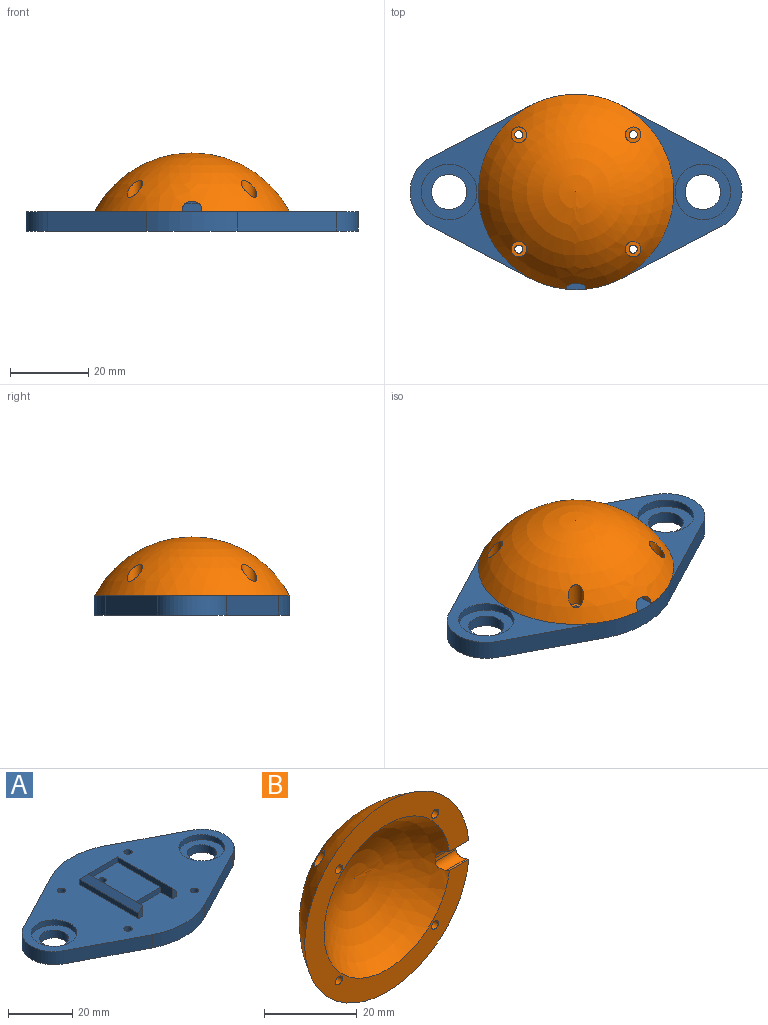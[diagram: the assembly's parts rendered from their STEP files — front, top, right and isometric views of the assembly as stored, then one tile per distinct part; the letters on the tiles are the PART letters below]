
ASSEMBLY  parts=2 mates=1
PART A: 69 faces, bbox 85x50x9 mm
  f0: cylinder r=1.25mm len=5mm, axis (0,0,1), area 39.3mm2, adj f57,f65
  f1: cylinder r=1.25mm len=3mm, axis (0,0,1), area 23.6mm2, adj f5,f50
  f2: cylinder r=1.25mm len=3mm, axis (0,0,1), area 23.6mm2, adj f5,f43
  f3: cylinder r=1.25mm len=3mm, axis (0,0,1), area 23.6mm2, adj f5,f36
  f4: cylinder r=1.25mm len=3mm, axis (0,0,1), area 23.6mm2, adj f5,f29
  f5: plane 85x50mm, normal (0,0,1), area 2120.5mm2, adj f1,f2,f3,f4,f6,f7,f8,f9
  f6: plane 25.58x13.31mm, normal (-0.46,-0.89,0), area 144.2mm2, adj f5,f7,f13,f14
  f7: cylinder r=25mm len=23.08mm, axis (0,0,-1), area 119.9mm2, adj f5,f6,f8,f14
  f8: plane 25.58x13.31mm, normal (0.46,-0.89,0), area 144.2mm2, adj f5,f7,f9,f14
  f9: cylinder r=10mm len=17.74mm, axis (0,0,-1), area 109.1mm2, adj f5,f8,f10,f14
  f10: plane 25.58x13.31mm, normal (0.46,0.89,0), area 144.2mm2, adj f5,f9,f11,f14
  f11: cylinder r=25mm len=23.08mm, axis (0,0,-1), area 119.9mm2, adj f5,f10,f12,f14
  f12: plane 25.58x13.31mm, normal (-0.46,0.89,0), area 144.2mm2, adj f5,f11,f13,f14
  f13: cylinder r=10mm len=17.74mm, axis (0,0,-1), area 109.1mm2, adj f5,f6,f12,f14
  f14: plane 85x50mm, normal (0,0,-1), area 2621.2mm2, adj f6,f7,f8,f9,f10,f11,f12,f13
  f15: cylinder r=4.5mm len=9mm, axis (0,0,1), area 84.8mm2, adj f14,f16
  f16: plane 14.25x14.25mm, normal (0,0,1), area 95.9mm2, adj f15,f17
  f17: cylinder r=7.12mm len=14.25mm, axis (0,0,1), area 89.5mm2, adj f5,f16
  f18: cylinder r=4.5mm len=9mm, axis (0,0,1), area 84.8mm2, adj f14,f19
  f19: plane 14.25x14.25mm, normal (0,0,1), area 95.9mm2, adj f18,f20
  f20: cylinder r=7.12mm len=14.25mm, axis (0,0,1), area 89.5mm2, adj f5,f19
  f21: plane 24x4mm, normal (1,0,0), area 58mm2, adj f5,f22,f28,f64,f65,f66
  f22: plane 13x2mm, normal (0,-1,0), area 26mm2, adj f21,f23,f65,f68
  f23: plane 24x4mm, normal (-1,0,0), area 58mm2, adj f5,f22,f24,f64,f65,f67
  f24: plane 4x2mm, normal (0,-1,0), area 6mm2, adj f5,f23,f25,f67
  f25: plane 26x2mm, normal (1,0,0), area 52mm2, adj f5,f24,f26,f67
  f26: plane 17x2mm, normal (0,1,0), area 34mm2, adj f5,f25,f27,f68
  f27: plane 26x2mm, normal (-1,0,0), area 52mm2, adj f5,f26,f28,f66
  f28: plane 4x2mm, normal (0,-1,0), area 6mm2, adj f5,f21,f27,f66
  f29: plane 5.2x4.5mm, normal (0,0,-1), area 12.6mm2, adj f4,f30,f31,f32,f33,f34,f35
  f30: plane 2.25x2mm, normal (-0.5,-0.87,0), area 5.2mm2, adj f14,f29,f31,f35
  f31: plane 2.6x2mm, normal (-1,0,0), area 5.2mm2, adj f14,f29,f30,f32
  f32: plane 2.25x2mm, normal (-0.5,0.87,0), area 5.2mm2, adj f14,f29,f31,f33
  f33: plane 2.25x2mm, normal (0.5,0.87,0), area 5.2mm2, adj f14,f29,f32,f34
  f34: plane 2.6x2mm, normal (1,0,0), area 5.2mm2, adj f14,f29,f33,f35
  f35: plane 2.25x2mm, normal (0.5,-0.87,0), area 5.2mm2, adj f14,f29,f30,f34
  f36: plane 5.2x4.5mm, normal (0,0,-1), area 12.6mm2, adj f3,f37,f38,f39,f40,f41,f42
  f37: plane 2.25x2mm, normal (-0.5,-0.87,0), area 5.2mm2, adj f14,f36,f38,f42
  f38: plane 2.6x2mm, normal (-1,0,0), area 5.2mm2, adj f14,f36,f37,f39
  f39: plane 2.25x2mm, normal (-0.5,0.87,0), area 5.2mm2, adj f14,f36,f38,f40
  f40: plane 2.25x2mm, normal (0.5,0.87,0), area 5.2mm2, adj f14,f36,f39,f41
  f41: plane 2.6x2mm, normal (1,0,0), area 5.2mm2, adj f14,f36,f40,f42
  f42: plane 2.25x2mm, normal (0.5,-0.87,0), area 5.2mm2, adj f14,f36,f37,f41
  f43: plane 5.2x4.5mm, normal (0,0,-1), area 12.6mm2, adj f2,f44,f45,f46,f47,f48,f49
  f44: plane 2.25x2mm, normal (-0.5,-0.87,0), area 5.2mm2, adj f14,f43,f45,f49
  f45: plane 2.6x2mm, normal (-1,0,0), area 5.2mm2, adj f14,f43,f44,f46
  f46: plane 2.25x2mm, normal (-0.5,0.87,0), area 5.2mm2, adj f14,f43,f45,f47
  f47: plane 2.25x2mm, normal (0.5,0.87,0), area 5.2mm2, adj f14,f43,f46,f48
  f48: plane 2.6x2mm, normal (1,0,0), area 5.2mm2, adj f14,f43,f47,f49
  f49: plane 2.25x2mm, normal (0.5,-0.87,0), area 5.2mm2, adj f14,f43,f44,f48
  f50: plane 5.2x4.5mm, normal (0,0,-1), area 12.6mm2, adj f1,f51,f52,f53,f54,f55,f56
  f51: plane 2.25x2mm, normal (-0.5,-0.87,0), area 5.2mm2, adj f14,f50,f52,f56
  f52: plane 2.6x2mm, normal (-1,0,0), area 5.2mm2, adj f14,f50,f51,f53
  f53: plane 2.25x2mm, normal (-0.5,0.87,0), area 5.2mm2, adj f14,f50,f52,f54
  f54: plane 2.25x2mm, normal (0.5,0.87,0), area 5.2mm2, adj f14,f50,f53,f55
  f55: plane 2.6x2mm, normal (1,0,0), area 5.2mm2, adj f14,f50,f54,f56
  f56: plane 2.25x2mm, normal (0.5,-0.87,0), area 5.2mm2, adj f14,f50,f51,f55
  f57: plane 5.2x4.5mm, normal (0,0,-1), area 12.6mm2, adj f0,f58,f59,f60,f61,f62,f63
  f58: plane 2.25x2mm, normal (-0.5,-0.87,0), area 5.2mm2, adj f14,f57,f59,f63
  f59: plane 2.6x2mm, normal (-1,0,0), area 5.2mm2, adj f14,f57,f58,f60
  f60: plane 2.25x2mm, normal (-0.5,0.87,0), area 5.2mm2, adj f14,f57,f59,f61
  f61: plane 2.25x2mm, normal (0.5,0.87,0), area 5.2mm2, adj f14,f57,f60,f62
  f62: plane 2.6x2mm, normal (1,0,0), area 5.2mm2, adj f14,f57,f61,f63
  f63: plane 2.25x2mm, normal (0.5,-0.87,0), area 5.2mm2, adj f14,f57,f58,f62
  f64: plane 13x2mm, normal (0,-1,0), area 26mm2, adj f5,f21,f23,f65
  f65: plane 19x13mm, normal (0,0,1), area 242.1mm2, adj f0,f21,f22,f23,f64
  f66: plane 26x2mm, normal (-0.71,0,0.71), area 70.7mm2, adj f21,f27,f28,f68
  f67: plane 26x2mm, normal (0.71,0,0.71), area 70.7mm2, adj f23,f24,f25,f68
  f68: plane 17x2mm, normal (0,0.71,0.71), area 42.4mm2, adj f22,f26,f66,f67
PART B: 20 faces, bbox 50x15x50 mm
  f0: sphere r=28.33mm, area 2583.7mm2, adj f2,f3,f6,f9,f12,f15,f16,f17
  f1: sphere r=23.33mm, area 1452.3mm2, adj f2,f15,f16,f17,f18,f19
  f2: plane 50x49.87mm, normal (0,-1,0), area 768.4mm2, adj f0,f1,f4,f7,f10,f13,f16,f17
  f3: cylinder r=2mm len=5.95mm, axis (0,1,0), area 48.4mm2, adj f0,f5
  f4: cylinder r=1.05mm len=2.1mm, axis (0,1,0), area 13.2mm2, adj f2,f5
  f5: plane 4x4mm, normal (0,1,0), area 9.1mm2, adj f3,f4
  f6: cylinder r=2mm len=5.95mm, axis (0,1,0), area 48.4mm2, adj f0,f8
  f7: cylinder r=1.05mm len=2.1mm, axis (0,1,0), area 13.2mm2, adj f2,f8
  f8: plane 4x4mm, normal (0,1,0), area 9.1mm2, adj f6,f7
  f9: cylinder r=2mm len=5.95mm, axis (0,1,0), area 48.4mm2, adj f0,f11
  f10: cylinder r=1.05mm len=2.1mm, axis (0,1,0), area 13.2mm2, adj f2,f11
  f11: plane 4x4mm, normal (0,1,0), area 9.1mm2, adj f9,f10
  f12: cylinder r=2mm len=5.95mm, axis (0,1,0), area 48.3mm2, adj f0,f14
  f13: cylinder r=1.05mm len=2.1mm, axis (0,1,0), area 13.2mm2, adj f2,f14
  f14: plane 4x4mm, normal (0,1,0), area 9.1mm2, adj f12,f13
  f15: plane 6.36x1mm, normal (0,-1,0), area 6.4mm2, adj f0,f1,f18,f19
  f16: plane 6.25x0.5mm, normal (0,0,1), area 3mm2, adj f0,f1,f2,f18
  f17: plane 6.25x0.5mm, normal (0,0,-1), area 3mm2, adj f0,f1,f2,f19
  f18: cylinder r=2mm len=7.47mm, axis (-1,0,0), area 19.5mm2, adj f0,f1,f15,f16
  f19: cylinder r=2mm len=7.47mm, axis (1,0,0), area 19.5mm2, adj f0,f1,f15,f17
PLACE A t=(-17.5,-6.1,-1.5)mm fixed
PLACE B rot(axis=(0.58,-0.58,-0.58),120deg) t=(-17.5,-6.1,-9.84)mm
MATE planar A.f5 <-> B.f2  axis (0,0,1) through (-17.5,-6.43,3.5)mm
